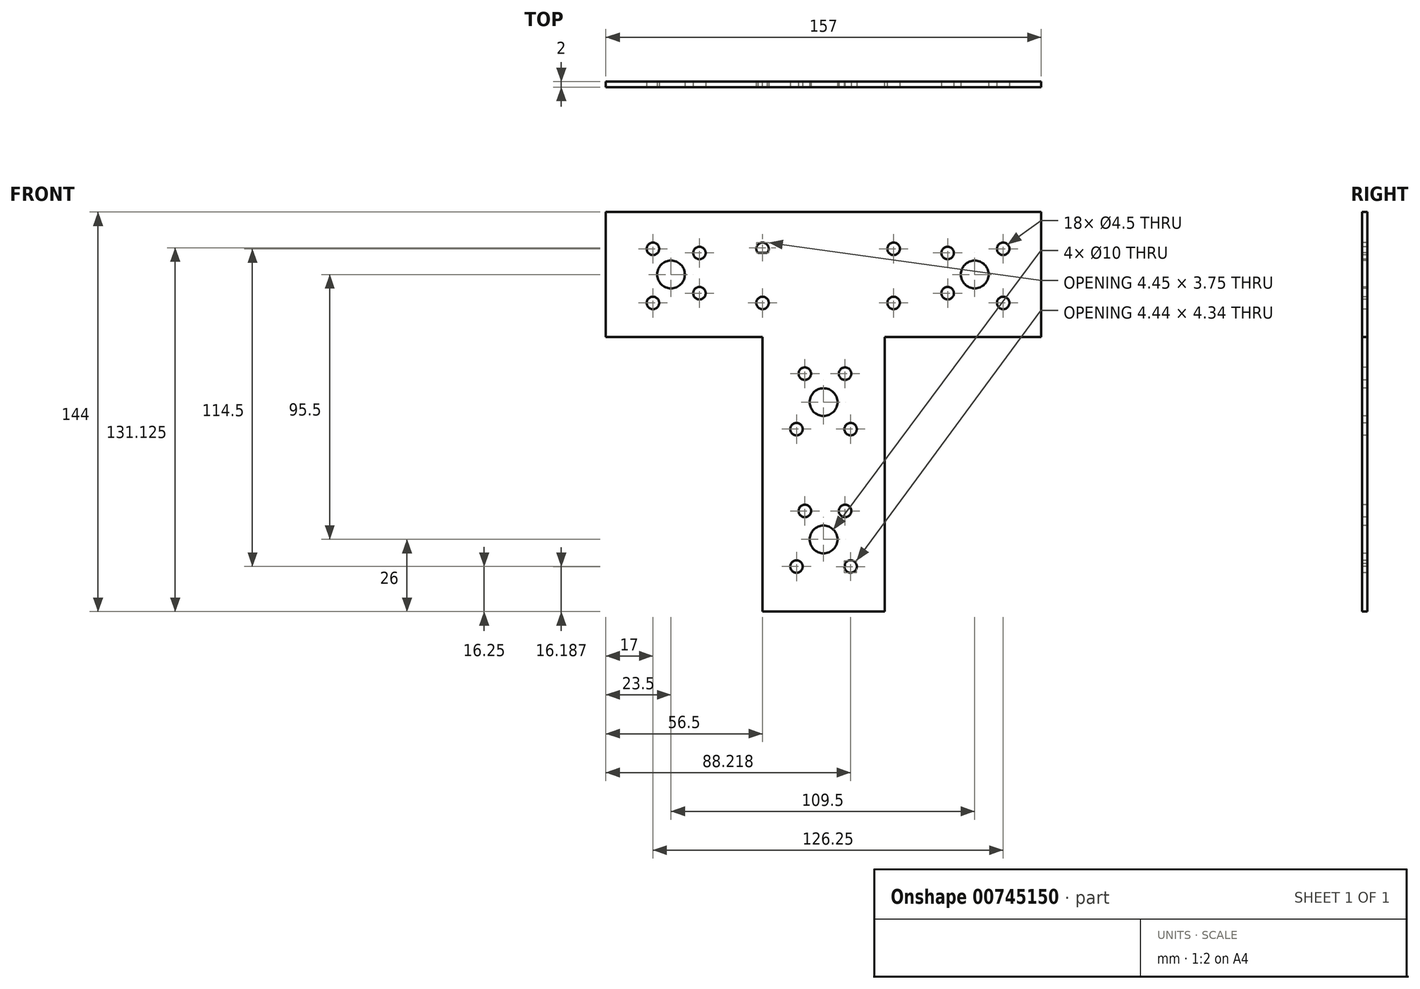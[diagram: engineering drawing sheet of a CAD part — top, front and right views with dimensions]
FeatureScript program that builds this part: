
annotation { "Feature Type Name" : "Feature", "Feature Type Description" : "" }
export const myFeature = defineFeature(function(context is Context, id is Id, definition is map)
    precondition{}
    {
        {
            var Q0;
            Q0=qCreatedBy(makeId("Front.planeOp"),FACE);
            var sketch = newSketch(context, id + "F0", { "sketchPlane" : qUnion([Q0])});
            skLineSegment(sketch, "E0.bottom", {"start": v(-78.5, -22.5) * mm, "end": v(78.5, -22.5) * mm});
            skLineSegment(sketch, "E0.top", {"start": v(-78.5, 22.5) * mm, "end": v(78.5, 22.5) * mm});
            skLineSegment(sketch, "E0.left", {"start": v(-78.5, -22.5) * mm, "end": v(-78.5, 22.5) * mm});
            skLineSegment(sketch, "E0.right", {"start": v(78.5, -22.5) * mm, "end": v(78.5, 22.5) * mm});
            skPoint(sketch, "E0.middle", {"position": v(0, 0) * mm});
            skLineSegment(sketch, "E1", {"start": v(-78.5, -22.5) * mm, "end": v(-22, -22.5) * mm});
            skLineSegment(sketch, "E2", {"start": v(-22, -22.5) * mm, "end": v(22, -22.5) * mm});
            skLineSegment(sketch, "E3", {"start": v(22, -22.5) * mm, "end": v(78.5, -22.5) * mm});
            skLineSegment(sketch, "E4", {"start": v(-22, -22.5) * mm, "end": v(-22, -121.5) * mm});
            skLineSegment(sketch, "E5", {"start": v(-22, -121.5) * mm, "end": v(22, -121.5) * mm});
            skLineSegment(sketch, "E6", {"start": v(22, -121.5) * mm, "end": v(22, -22.5) * mm});
            skSolve(sketch);
        }
        {
            var Q0;
            Q0 = qSketchRegion(id + "F0", true);
            extrude(context, id + "F1", {"entities" : qUnion([Q0]), "depth" : 2 * mm, "offsetDistance" : 25.4 * mm});
        }
        {
            var Q0;
            Q0=makeQuery(id+"F1.opExtrude","CAP_FACE",FACE,{"disambiguationData":[OSD([sQuery(id+"F0.wireOp",EDGE,"E0.top"),sQuery(id+"F0.wireOp",EDGE,"E0.left"),sQuery(id+"F0.wireOp",EDGE,"E0.right"),sQuery(id+"F0.wireOp",EDGE,"E1"),sQuery(id+"F0.wireOp",EDGE,"E3"),sQuery(id+"F0.wireOp",EDGE,"E4"),sQuery(id+"F0.wireOp",EDGE,"E5"),sQuery(id+"F0.wireOp",EDGE,"E6")])],"isStart":false});
            var sketch = newSketch(context, id + "F2", { "sketchPlane" : qUnion([Q0])});
            skLineSegment(sketch, "E7", {"start": v(9.75, -121.5) * mm, "end": v(9.75, -105.25) * mm});
            skLineSegment(sketch, "E8", {"start": v(9.75, -105.25) * mm, "end": v(22, -105.25) * mm});
            skCircle(sketch, "E9", {"center": v(9.75, -105.25) * mm, "radius": 2.25 * mm});
            skLineSegment(sketch, "E10", {"start": v(9.75, -105.25) * mm, "end": v(-9.75, -105.25) * mm});
            skCircle(sketch, "E11", {"center": v(-9.75, -105.25) * mm, "radius": 2.25 * mm});
            skLineSegment(sketch, "E12", {"start": v(22, -95.5) * mm, "end": v(0, -95.5) * mm});
            skLineSegment(sketch, "E13", {"start": v(0, -95.5) * mm, "end": v(0, -121.5) * mm});
            skCircle(sketch, "E14", {"center": v(0, -95.5) * mm, "radius": 5 * mm});
            skLineSegment(sketch, "E15", {"start": v(22, -85.25) * mm, "end": v(7.75, -85.25) * mm});
            skLineSegment(sketch, "E16", {"start": v(7.75, -85.25) * mm, "end": v(7.75, -121.5) * mm});
            skCircle(sketch, "E17", {"center": v(7.75, -85.25) * mm, "radius": 2.25 * mm});
            skLineSegment(sketch, "E18", {"start": v(7.75, -85.25) * mm, "end": v(-6.75, -85.25) * mm});
            skCircle(sketch, "E19", {"center": v(-6.75, -85.25) * mm, "radius": 2.25 * mm});
            skLineSegment(sketch, "E20", {"start": v(9.75, -105.25) * mm, "end": v(9.75, -55.75) * mm});
            skCircle(sketch, "E21", {"center": v(9.75, -55.75) * mm, "radius": 2.25 * mm});
            skLineSegment(sketch, "E22", {"start": v(9.75, -55.75) * mm, "end": v(-9.75, -55.75) * mm});
            skCircle(sketch, "E23", {"center": v(-9.75, -55.75) * mm, "radius": 2.25 * mm});
            skLineSegment(sketch, "E24", {"start": v(0, -95.5) * mm, "end": v(0, -46) * mm});
            skCircle(sketch, "E25", {"center": v(0, -46) * mm, "radius": 5 * mm});
            skLineSegment(sketch, "E26", {"start": v(7.75, -85.25) * mm, "end": v(7.75, -35.75) * mm});
            skCircle(sketch, "E27", {"center": v(7.75, -35.75) * mm, "radius": 2.25 * mm});
            skLineSegment(sketch, "E28", {"start": v(7.75, -35.75) * mm, "end": v(-6.75, -35.75) * mm});
            skCircle(sketch, "E29", {"center": v(-6.75, -35.75) * mm, "radius": 2.25 * mm});
            skLineSegment(sketch, "E30", {"start": v(78.5, -10.25) * mm, "end": v(64.75, -10.25) * mm});
            skLineSegment(sketch, "E31", {"start": v(64.75, -10.25) * mm, "end": v(64.75, -22.5) * mm});
            skCircle(sketch, "E32", {"center": v(64.75, -10.25) * mm, "radius": 2.25 * mm});
            skLineSegment(sketch, "E33", {"start": v(64.75, -10.25) * mm, "end": v(64.75, 9.25) * mm});
            skCircle(sketch, "E34", {"center": v(64.75, 9.25) * mm, "radius": 2.25 * mm});
            skLineSegment(sketch, "E35", {"start": v(78.5, 0) * mm, "end": v(54.5, 0) * mm});
            skLineSegment(sketch, "E36", {"start": v(54.5, 0) * mm, "end": v(54.5, -22.5) * mm});
            skCircle(sketch, "E37", {"center": v(54.5, 0) * mm, "radius": 5 * mm});
            skLineSegment(sketch, "E38", {"start": v(78.5, 7.75) * mm, "end": v(44.75, 7.75) * mm});
            skCircle(sketch, "E39", {"center": v(44.75, 7.75) * mm, "radius": 2.25 * mm});
            skLineSegment(sketch, "E40", {"start": v(44.75, 7.75) * mm, "end": v(44.75, 22.5) * mm});
            skLineSegment(sketch, "E41", {"start": v(44.75, 7.75) * mm, "end": v(44.75, -6.75) * mm});
            skCircle(sketch, "E42", {"center": v(44.75, -6.75) * mm, "radius": 2.25 * mm});
            skLineSegment(sketch, "E43", {"start": v(64.75, 9.25) * mm, "end": v(25.25, 9.25) * mm});
            skCircle(sketch, "E44", {"center": v(25.25, 9.25) * mm, "radius": 2.25 * mm});
            skLineSegment(sketch, "E45", {"start": v(25.25, 9.25) * mm, "end": v(25.25, -10.25) * mm});
            skCircle(sketch, "E46", {"center": v(25.25, -10.25) * mm, "radius": 2.25 * mm});
            skLineSegment(sketch, "E47", {"start": v(25.25, 9.25) * mm, "end": v(-22, 9.25) * mm});
            skCircle(sketch, "E48", {"center": v(-22, 9.25) * mm, "radius": 2.25 * mm});
            skLineSegment(sketch, "E49", {"start": v(25.25, -10.25) * mm, "end": v(-22, -10.25) * mm});
            skCircle(sketch, "E50", {"center": v(-22, -10.25) * mm, "radius": 2.25 * mm});
            skLineSegment(sketch, "E51", {"start": v(-22, 9.25) * mm, "end": v(-61.5, 9.25) * mm});
            skCircle(sketch, "E52", {"center": v(-61.5, 9.25) * mm, "radius": 2.25 * mm});
            skLineSegment(sketch, "E53", {"start": v(-22, -10.25) * mm, "end": v(-61.5, -10.25) * mm});
            skCircle(sketch, "E54", {"center": v(-61.5, -10.25) * mm, "radius": 2.25 * mm});
            skLineSegment(sketch, "E55", {"start": v(44.75, 7.75) * mm, "end": v(-44.75, 7.75) * mm});
            skLineSegment(sketch, "E56", {"start": v(44.75, -6.75) * mm, "end": v(-44.75, -6.75) * mm});
            skCircle(sketch, "E57", {"center": v(-44.75, 7.75) * mm, "radius": 2.25 * mm});
            skCircle(sketch, "E58", {"center": v(-44.75, -6.75) * mm, "radius": 2.25 * mm});
            skLineSegment(sketch, "E59", {"start": v(54.5, 0) * mm, "end": v(-55, 0) * mm});
            skCircle(sketch, "E60", {"center": v(-55, 0) * mm, "radius": 5 * mm});
            skSolve(sketch);
        }
        {
            var Q0;
            Q0=makeQuery(id+"F2.imprint","IMPRINT",FACE,{"disambiguationData":[TD([[makeQuery(id+"F2.imprint","IMPRINT",EDGE,{"derivedFrom":sQuery(id+"F2.wireOp",EDGE,"E11")}),1.0]])]});
            var Q1;
            Q1=makeQuery(id+"F2.imprint","IMPRINT",FACE,{"disambiguationData":[TD([[makeQuery(id+"F2.imprint","IMPRINT",EDGE,{"derivedFrom":sQuery(id+"F2.wireOp",EDGE,"E19")}),1.0]])]});
            var Q2;
            Q2=makeQuery(id+"F2.imprint","IMPRINT",FACE,{"disambiguationData":[TD([[makeQuery(id+"F2.imprint","IMPRINT",EDGE,{"derivedFrom":sQuery(id+"F2.wireOp",EDGE,"E23")}),1.0]])]});
            var Q3;
            Q3=makeQuery(id+"F2.imprint","IMPRINT",FACE,{"disambiguationData":[TD([[makeQuery(id+"F2.imprint","IMPRINT",EDGE,{"derivedFrom":sQuery(id+"F2.wireOp",EDGE,"E25")}),1.0]])]});
            var Q4;
            Q4=makeQuery(id+"F2.imprint","IMPRINT",FACE,{"disambiguationData":[TD([[makeQuery(id+"F2.imprint","IMPRINT",EDGE,{"derivedFrom":sQuery(id+"F2.wireOp",EDGE,"E29")}),1.0]])]});
            var Q5;
            Q5=makeQuery(id+"F2.imprint","IMPRINT",FACE,{"disambiguationData":[TD([[makeQuery(id+"F2.imprint","IMPRINT",EDGE,{"derivedFrom":sQuery(id+"F2.wireOp",EDGE,"E52")}),1.0]])]});
            var Q6;
            Q6=makeQuery(id+"F2.imprint","IMPRINT",FACE,{"disambiguationData":[TD([[makeQuery(id+"F2.imprint","IMPRINT",EDGE,{"derivedFrom":sQuery(id+"F2.wireOp",EDGE,"E54")}),1.0]])]});
            var Q7;
            Q7=makeQuery(id+"F2.imprint","IMPRINT",FACE,{"disambiguationData":[TD([[makeQuery(id+"F2.imprint","IMPRINT",EDGE,{"derivedFrom":sQuery(id+"F2.wireOp",EDGE,"E58")}),1.0]])]});
            var Q8;
            Q8=makeQuery(id+"F2.imprint","IMPRINT",FACE,{"disambiguationData":[TD([[makeQuery(id+"F2.imprint","IMPRINT",EDGE,{"derivedFrom":sQuery(id+"F2.wireOp",EDGE,"E60")}),1.0]])]});
            var Q9;
            {var subQ0=sQuery(id+"F2.wireOp",EDGE,"E28");var subQ1=sQuery(id+"F2.wireOp",EDGE,"E26");var subQ2=makeQuery(id+"F2.imprint","INTERSECT",VERTEX,{"derivedFrom":[subQ1,subQ0]});Q9=makeQuery(id+"F2.imprint","IMPRINT",FACE,{"disambiguationData":[TD([[makeQuery(id+"F2.imprint","IMPRINT",EDGE,{"disambiguationData":[TD([[subQ2,1.0]])],"derivedFrom":subQ1}),1.0]])]});}
            var Q10;
            {var subQ0=sQuery(id+"F2.wireOp",EDGE,"E28");var subQ1=sQuery(id+"F2.wireOp",EDGE,"E26");var subQ2=makeQuery(id+"F2.imprint","INTERSECT",VERTEX,{"derivedFrom":[subQ1,subQ0]});Q10=makeQuery(id+"F2.imprint","IMPRINT",FACE,{"disambiguationData":[TD([[makeQuery(id+"F2.imprint","IMPRINT",EDGE,{"disambiguationData":[TD([[subQ2,1.0]])],"derivedFrom":subQ1}),-1.0]])]});}
            var Q11;
            {var subQ0=sQuery(id+"F2.wireOp",EDGE,"E56");var subQ1=sQuery(id+"F2.wireOp",EDGE,"E41");var subQ2=makeQuery(id+"F2.imprint","INTERSECT",VERTEX,{"derivedFrom":[subQ1,subQ0]});Q11=makeQuery(id+"F2.imprint","IMPRINT",FACE,{"disambiguationData":[TD([[makeQuery(id+"F2.imprint","IMPRINT",EDGE,{"disambiguationData":[TD([[subQ2,1.0]])],"derivedFrom":subQ1}),-1.0]])]});}
            var Q12;
            {var subQ0=sQuery(id+"F2.wireOp",EDGE,"E56");var subQ1=sQuery(id+"F2.wireOp",EDGE,"E41");var subQ2=makeQuery(id+"F2.imprint","INTERSECT",VERTEX,{"derivedFrom":[subQ1,subQ0]});Q12=makeQuery(id+"F2.imprint","IMPRINT",FACE,{"disambiguationData":[TD([[makeQuery(id+"F2.imprint","IMPRINT",EDGE,{"disambiguationData":[TD([[subQ2,1.0]])],"derivedFrom":subQ1}),1.0]])]});}
            var Q13;
            {var subQ0=sQuery(id+"F2.wireOp",EDGE,"E49");var subQ1=sQuery(id+"F2.wireOp",EDGE,"E45");var subQ2=makeQuery(id+"F2.imprint","INTERSECT",VERTEX,{"derivedFrom":[subQ1,subQ0]});Q13=makeQuery(id+"F2.imprint","IMPRINT",FACE,{"disambiguationData":[TD([[makeQuery(id+"F2.imprint","IMPRINT",EDGE,{"disambiguationData":[TD([[subQ2,1.0]])],"derivedFrom":subQ1}),-1.0]])]});}
            var Q14;
            {var subQ0=sQuery(id+"F2.wireOp",EDGE,"E49");var subQ1=sQuery(id+"F2.wireOp",EDGE,"E45");var subQ2=makeQuery(id+"F2.imprint","INTERSECT",VERTEX,{"derivedFrom":[subQ1,subQ0]});Q14=makeQuery(id+"F2.imprint","IMPRINT",FACE,{"disambiguationData":[TD([[makeQuery(id+"F2.imprint","IMPRINT",EDGE,{"disambiguationData":[TD([[subQ2,1.0]])],"derivedFrom":subQ1}),1.0]])]});}
            var Q15;
            {var subQ0=sQuery(id+"F2.wireOp",EDGE,"E51");var subQ1=sQuery(id+"F2.wireOp",EDGE,"E47");var subQ2=makeQuery(id+"F2.imprint","INTERSECT",VERTEX,{"derivedFrom":[subQ1,subQ0]});Q15=makeQuery(id+"F2.imprint","IMPRINT",FACE,{"disambiguationData":[TD([[makeQuery(id+"F2.imprint","IMPRINT",EDGE,{"disambiguationData":[TD([[subQ2,1.0]])],"derivedFrom":subQ1}),-1.0]])]});}
            var Q16;
            {var subQ0=sQuery(id+"F2.wireOp",EDGE,"E55");var subQ1=sQuery(id+"F2.wireOp",EDGE,"E48");var subQ2=makeQuery(id+"F2.imprint","INTERSECT",VERTEX,{"disambiguationData":[OD(0.0)],"derivedFrom":[subQ1,subQ0]});Q16=makeQuery(id+"F2.imprint","IMPRINT",FACE,{"disambiguationData":[TD([[makeQuery(id+"F2.imprint","IMPRINT",EDGE,{"disambiguationData":[TD([[subQ2,-1.0]])],"derivedFrom":subQ1}),1.0]])]});}
            var Q17;
            {var subQ0=sQuery(id+"F2.wireOp",EDGE,"E53");var subQ1=sQuery(id+"F2.wireOp",EDGE,"E49");var subQ2=makeQuery(id+"F2.imprint","INTERSECT",VERTEX,{"derivedFrom":[subQ1,subQ0]});Q17=makeQuery(id+"F2.imprint","IMPRINT",FACE,{"disambiguationData":[TD([[makeQuery(id+"F2.imprint","IMPRINT",EDGE,{"disambiguationData":[TD([[subQ2,1.0]])],"derivedFrom":subQ1}),-1.0]])]});}
            var Q18;
            {var subQ0=sQuery(id+"F2.wireOp",EDGE,"E53");var subQ1=sQuery(id+"F2.wireOp",EDGE,"E49");var subQ2=makeQuery(id+"F2.imprint","INTERSECT",VERTEX,{"derivedFrom":[subQ1,subQ0]});Q18=makeQuery(id+"F2.imprint","IMPRINT",FACE,{"disambiguationData":[TD([[makeQuery(id+"F2.imprint","IMPRINT",EDGE,{"disambiguationData":[TD([[subQ2,1.0]])],"derivedFrom":subQ1}),1.0]])]});}
            var Q19;
            {var subQ0=sQuery(id+"F2.wireOp",EDGE,"E57");var subQ1=sQuery(id+"F2.wireOp",EDGE,"E51");var subQ2=makeQuery(id+"F2.imprint","INTERSECT",VERTEX,{"disambiguationData":[OD(0.0)],"derivedFrom":[subQ1,subQ0]});Q19=makeQuery(id+"F2.imprint","IMPRINT",FACE,{"disambiguationData":[TD([[makeQuery(id+"F2.imprint","IMPRINT",EDGE,{"disambiguationData":[TD([[subQ2,1.0]])],"derivedFrom":subQ1}),-1.0]])]});}
            var Q20;
            {var subQ1=sQuery(id+"F2.wireOp",EDGE,"E7");var subQ3=sQuery(id+"F2.wireOp",EDGE,"E9");var subQ4=makeQuery(id+"F2.imprint","INTERSECT",VERTEX,{"derivedFrom":[subQ1,subQ3]});Q20=makeQuery(id+"F2.imprint","IMPRINT",FACE,{"disambiguationData":[TD([[makeQuery(id+"F2.imprint","IMPRINT",EDGE,{"disambiguationData":[TD([[subQ4,-1.0]])],"derivedFrom":subQ3}),1.0]])]});}
            var Q21;
            {var subQ1=sQuery(id+"F2.wireOp",EDGE,"E8");var subQ3=sQuery(id+"F2.wireOp",EDGE,"E9");var subQ4=makeQuery(id+"F2.imprint","INTERSECT",VERTEX,{"derivedFrom":[subQ1,subQ3]});Q21=makeQuery(id+"F2.imprint","IMPRINT",FACE,{"disambiguationData":[TD([[makeQuery(id+"F2.imprint","IMPRINT",EDGE,{"disambiguationData":[TD([[subQ4,-1.0]])],"derivedFrom":subQ3}),1.0]])]});}
            var Q22;
            {var subQ0=sQuery(id+"F2.wireOp",EDGE,"E16");var subQ1=sQuery(id+"F2.wireOp",EDGE,"E9");var subQ2=makeQuery(id+"F2.imprint","INTERSECT",VERTEX,{"disambiguationData":[OD(0.0)],"derivedFrom":[subQ1,subQ0]});Q22=makeQuery(id+"F2.imprint","IMPRINT",FACE,{"disambiguationData":[TD([[makeQuery(id+"F2.imprint","IMPRINT",EDGE,{"disambiguationData":[TD([[subQ2,-1.0]])],"derivedFrom":subQ1}),1.0]])]});}
            var Q23;
            {var subQ0=sQuery(id+"F2.wireOp",EDGE,"E10");var subQ1=sQuery(id+"F2.wireOp",EDGE,"E9");var subQ2=makeQuery(id+"F2.imprint","INTERSECT",VERTEX,{"derivedFrom":[subQ1,subQ0]});Q23=makeQuery(id+"F2.imprint","IMPRINT",FACE,{"disambiguationData":[TD([[makeQuery(id+"F2.imprint","IMPRINT",EDGE,{"disambiguationData":[TD([[subQ2,-1.0]])],"derivedFrom":subQ1}),1.0]])]});}
            var Q24;
            {var subQ1=sQuery(id+"F2.wireOp",EDGE,"E12");var subQ3=sQuery(id+"F2.wireOp",EDGE,"E14");var subQ4=makeQuery(id+"F2.imprint","INTERSECT",VERTEX,{"derivedFrom":[subQ1,subQ3]});Q24=makeQuery(id+"F2.imprint","IMPRINT",FACE,{"disambiguationData":[TD([[makeQuery(id+"F2.imprint","IMPRINT",EDGE,{"disambiguationData":[TD([[subQ4,1.0]])],"derivedFrom":subQ3}),1.0]])]});}
            var Q25;
            {var subQ1=sQuery(id+"F2.wireOp",EDGE,"E12");var subQ3=sQuery(id+"F2.wireOp",EDGE,"E14");var subQ4=makeQuery(id+"F2.imprint","INTERSECT",VERTEX,{"derivedFrom":[subQ1,subQ3]});Q25=makeQuery(id+"F2.imprint","IMPRINT",FACE,{"disambiguationData":[TD([[makeQuery(id+"F2.imprint","IMPRINT",EDGE,{"disambiguationData":[TD([[subQ4,-1.0]])],"derivedFrom":subQ3}),1.0]])]});}
            var Q26;
            {var subQ1=sQuery(id+"F2.wireOp",EDGE,"E13");var subQ3=sQuery(id+"F2.wireOp",EDGE,"E14");var subQ4=makeQuery(id+"F2.imprint","INTERSECT",VERTEX,{"derivedFrom":[subQ1,subQ3]});Q26=makeQuery(id+"F2.imprint","IMPRINT",FACE,{"disambiguationData":[TD([[makeQuery(id+"F2.imprint","IMPRINT",EDGE,{"disambiguationData":[TD([[subQ4,1.0]])],"derivedFrom":subQ3}),1.0]])]});}
            var Q27;
            {var subQ0=sQuery(id+"F2.wireOp",EDGE,"E17");var subQ1=sQuery(id+"F2.wireOp",EDGE,"E15");var subQ2=makeQuery(id+"F2.imprint","INTERSECT",VERTEX,{"derivedFrom":[subQ1,subQ0]});Q27=makeQuery(id+"F2.imprint","IMPRINT",FACE,{"disambiguationData":[TD([[makeQuery(id+"F2.imprint","IMPRINT",EDGE,{"disambiguationData":[TD([[subQ2,-1.0]])],"derivedFrom":subQ1}),-1.0]])]});}
            var Q28;
            {var subQ0=sQuery(id+"F2.wireOp",EDGE,"E17");var subQ1=sQuery(id+"F2.wireOp",EDGE,"E15");var subQ2=makeQuery(id+"F2.imprint","INTERSECT",VERTEX,{"derivedFrom":[subQ1,subQ0]});Q28=makeQuery(id+"F2.imprint","IMPRINT",FACE,{"disambiguationData":[TD([[makeQuery(id+"F2.imprint","IMPRINT",EDGE,{"disambiguationData":[TD([[subQ2,-1.0]])],"derivedFrom":subQ1}),1.0]])]});}
            var Q29;
            {var subQ0=sQuery(id+"F2.wireOp",EDGE,"E22");var subQ1=sQuery(id+"F2.wireOp",EDGE,"E20");var subQ2=makeQuery(id+"F2.imprint","INTERSECT",VERTEX,{"derivedFrom":[subQ1,subQ0]});Q29=makeQuery(id+"F2.imprint","IMPRINT",FACE,{"disambiguationData":[TD([[makeQuery(id+"F2.imprint","IMPRINT",EDGE,{"disambiguationData":[TD([[subQ2,1.0]])],"derivedFrom":subQ1}),1.0]])]});}
            var Q30;
            {var subQ0=sQuery(id+"F2.wireOp",EDGE,"E22");var subQ1=sQuery(id+"F2.wireOp",EDGE,"E20");var subQ2=makeQuery(id+"F2.imprint","INTERSECT",VERTEX,{"derivedFrom":[subQ1,subQ0]});Q30=makeQuery(id+"F2.imprint","IMPRINT",FACE,{"disambiguationData":[TD([[makeQuery(id+"F2.imprint","IMPRINT",EDGE,{"disambiguationData":[TD([[subQ2,1.0]])],"derivedFrom":subQ1}),-1.0]])]});}
            var Q31;
            {var subQ0=sQuery(id+"F2.wireOp",EDGE,"E26");var subQ1=sQuery(id+"F2.wireOp",EDGE,"E21");var subQ2=makeQuery(id+"F2.imprint","INTERSECT",VERTEX,{"disambiguationData":[OD(0.0)],"derivedFrom":[subQ1,subQ0]});Q31=makeQuery(id+"F2.imprint","IMPRINT",FACE,{"disambiguationData":[TD([[makeQuery(id+"F2.imprint","IMPRINT",EDGE,{"disambiguationData":[TD([[subQ2,-1.0]])],"derivedFrom":subQ1}),1.0]])]});}
            var Q32;
            {var subQ0=sQuery(id+"F2.wireOp",EDGE,"E22");var subQ1=sQuery(id+"F2.wireOp",EDGE,"E21");var subQ2=makeQuery(id+"F2.imprint","INTERSECT",VERTEX,{"derivedFrom":[subQ1,subQ0]});Q32=makeQuery(id+"F2.imprint","IMPRINT",FACE,{"disambiguationData":[TD([[makeQuery(id+"F2.imprint","IMPRINT",EDGE,{"disambiguationData":[TD([[subQ2,-1.0]])],"derivedFrom":subQ1}),1.0]])]});}
            var Q33;
            {var subQ1=sQuery(id+"F2.wireOp",EDGE,"E30");var subQ3=sQuery(id+"F2.wireOp",EDGE,"E32");var subQ4=makeQuery(id+"F2.imprint","INTERSECT",VERTEX,{"derivedFrom":[subQ1,subQ3]});Q33=makeQuery(id+"F2.imprint","IMPRINT",FACE,{"disambiguationData":[TD([[makeQuery(id+"F2.imprint","IMPRINT",EDGE,{"disambiguationData":[TD([[subQ4,1.0]])],"derivedFrom":subQ3}),1.0]])]});}
            var Q34;
            {var subQ1=sQuery(id+"F2.wireOp",EDGE,"E30");var subQ3=sQuery(id+"F2.wireOp",EDGE,"E32");var subQ4=makeQuery(id+"F2.imprint","INTERSECT",VERTEX,{"derivedFrom":[subQ1,subQ3]});Q34=makeQuery(id+"F2.imprint","IMPRINT",FACE,{"disambiguationData":[TD([[makeQuery(id+"F2.imprint","IMPRINT",EDGE,{"disambiguationData":[TD([[subQ4,-1.0]])],"derivedFrom":subQ3}),1.0]])]});}
            var Q35;
            {var subQ1=sQuery(id+"F2.wireOp",EDGE,"E31");var subQ3=sQuery(id+"F2.wireOp",EDGE,"E32");var subQ4=makeQuery(id+"F2.imprint","INTERSECT",VERTEX,{"derivedFrom":[subQ1,subQ3]});Q35=makeQuery(id+"F2.imprint","IMPRINT",FACE,{"disambiguationData":[TD([[makeQuery(id+"F2.imprint","IMPRINT",EDGE,{"disambiguationData":[TD([[subQ4,1.0]])],"derivedFrom":subQ3}),1.0]])]});}
            var Q36;
            {var subQ0=sQuery(id+"F2.wireOp",EDGE,"E34");var subQ1=sQuery(id+"F2.wireOp",EDGE,"E33");var subQ2=makeQuery(id+"F2.imprint","INTERSECT",VERTEX,{"derivedFrom":[subQ1,subQ0]});Q36=makeQuery(id+"F2.imprint","IMPRINT",FACE,{"disambiguationData":[TD([[makeQuery(id+"F2.imprint","IMPRINT",EDGE,{"disambiguationData":[TD([[subQ2,-1.0]])],"derivedFrom":subQ1}),1.0]])]});}
            var Q37;
            {var subQ0=sQuery(id+"F2.wireOp",EDGE,"E34");var subQ1=sQuery(id+"F2.wireOp",EDGE,"E33");var subQ2=makeQuery(id+"F2.imprint","INTERSECT",VERTEX,{"derivedFrom":[subQ1,subQ0]});Q37=makeQuery(id+"F2.imprint","IMPRINT",FACE,{"disambiguationData":[TD([[makeQuery(id+"F2.imprint","IMPRINT",EDGE,{"disambiguationData":[TD([[subQ2,-1.0]])],"derivedFrom":subQ1}),-1.0]])]});}
            var Q38;
            {var subQ0=sQuery(id+"F2.wireOp",EDGE,"E43");var subQ1=sQuery(id+"F2.wireOp",EDGE,"E33");var subQ2=makeQuery(id+"F2.imprint","INTERSECT",VERTEX,{"derivedFrom":[subQ1,subQ0]});Q38=makeQuery(id+"F2.imprint","IMPRINT",FACE,{"disambiguationData":[TD([[makeQuery(id+"F2.imprint","IMPRINT",EDGE,{"disambiguationData":[TD([[subQ2,1.0]])],"derivedFrom":subQ1}),1.0]])]});}
            var Q39;
            {var subQ0=sQuery(id+"F2.wireOp",EDGE,"E43");var subQ1=sQuery(id+"F2.wireOp",EDGE,"E33");var subQ2=makeQuery(id+"F2.imprint","INTERSECT",VERTEX,{"derivedFrom":[subQ1,subQ0]});Q39=makeQuery(id+"F2.imprint","IMPRINT",FACE,{"disambiguationData":[TD([[makeQuery(id+"F2.imprint","IMPRINT",EDGE,{"disambiguationData":[TD([[subQ2,1.0]])],"derivedFrom":subQ1}),-1.0]])]});}
            var Q40;
            {var subQ1=sQuery(id+"F2.wireOp",EDGE,"E35");var subQ3=sQuery(id+"F2.wireOp",EDGE,"E37");var subQ4=makeQuery(id+"F2.imprint","INTERSECT",VERTEX,{"derivedFrom":[subQ1,subQ3]});Q40=makeQuery(id+"F2.imprint","IMPRINT",FACE,{"disambiguationData":[TD([[makeQuery(id+"F2.imprint","IMPRINT",EDGE,{"disambiguationData":[TD([[subQ4,1.0]])],"derivedFrom":subQ3}),1.0]])]});}
            var Q41;
            {var subQ1=sQuery(id+"F2.wireOp",EDGE,"E35");var subQ3=sQuery(id+"F2.wireOp",EDGE,"E37");var subQ4=makeQuery(id+"F2.imprint","INTERSECT",VERTEX,{"derivedFrom":[subQ1,subQ3]});Q41=makeQuery(id+"F2.imprint","IMPRINT",FACE,{"disambiguationData":[TD([[makeQuery(id+"F2.imprint","IMPRINT",EDGE,{"disambiguationData":[TD([[subQ4,-1.0]])],"derivedFrom":subQ3}),1.0]])]});}
            var Q42;
            {var subQ1=sQuery(id+"F2.wireOp",EDGE,"E36");var subQ3=sQuery(id+"F2.wireOp",EDGE,"E37");var subQ4=makeQuery(id+"F2.imprint","INTERSECT",VERTEX,{"derivedFrom":[subQ1,subQ3]});Q42=makeQuery(id+"F2.imprint","IMPRINT",FACE,{"disambiguationData":[TD([[makeQuery(id+"F2.imprint","IMPRINT",EDGE,{"disambiguationData":[TD([[subQ4,1.0]])],"derivedFrom":subQ3}),1.0]])]});}
            var Q43;
            {var subQ0=sQuery(id+"F2.wireOp",EDGE,"E43");var subQ1=sQuery(id+"F2.wireOp",EDGE,"E39");var subQ2=makeQuery(id+"F2.imprint","INTERSECT",VERTEX,{"disambiguationData":[OD(0.0)],"derivedFrom":[subQ1,subQ0]});Q43=makeQuery(id+"F2.imprint","IMPRINT",FACE,{"disambiguationData":[TD([[makeQuery(id+"F2.imprint","IMPRINT",EDGE,{"disambiguationData":[TD([[subQ2,-1.0]])],"derivedFrom":subQ1}),1.0]])]});}
            var Q44;
            {var subQ0=sQuery(id+"F2.wireOp",EDGE,"E40");var subQ1=sQuery(id+"F2.wireOp",EDGE,"E39");var subQ2=makeQuery(id+"F2.imprint","INTERSECT",VERTEX,{"derivedFrom":[subQ1,subQ0]});Q44=makeQuery(id+"F2.imprint","IMPRINT",FACE,{"disambiguationData":[TD([[makeQuery(id+"F2.imprint","IMPRINT",EDGE,{"disambiguationData":[TD([[subQ2,-1.0]])],"derivedFrom":subQ1}),1.0]])]});}
            var Q45;
            {var subQ1=sQuery(id+"F2.wireOp",EDGE,"E43");var subQ3=sQuery(id+"F2.wireOp",EDGE,"E44");var subQ4=makeQuery(id+"F2.imprint","INTERSECT",VERTEX,{"derivedFrom":[subQ1,subQ3]});Q45=makeQuery(id+"F2.imprint","IMPRINT",FACE,{"disambiguationData":[TD([[makeQuery(id+"F2.imprint","IMPRINT",EDGE,{"disambiguationData":[TD([[subQ4,-1.0]])],"derivedFrom":subQ3}),1.0]])]});}
            var Q46;
            {var subQ0=sQuery(id+"F2.wireOp",EDGE,"E55");var subQ1=sQuery(id+"F2.wireOp",EDGE,"E44");var subQ2=makeQuery(id+"F2.imprint","INTERSECT",VERTEX,{"disambiguationData":[OD(0.0)],"derivedFrom":[subQ1,subQ0]});Q46=makeQuery(id+"F2.imprint","IMPRINT",FACE,{"disambiguationData":[TD([[makeQuery(id+"F2.imprint","IMPRINT",EDGE,{"disambiguationData":[TD([[subQ2,-1.0]])],"derivedFrom":subQ1}),1.0]])]});}
            var Q47;
            {var subQ0=sQuery(id+"F2.wireOp",EDGE,"E45");var subQ1=sQuery(id+"F2.wireOp",EDGE,"E44");var subQ2=makeQuery(id+"F2.imprint","INTERSECT",VERTEX,{"derivedFrom":[subQ1,subQ0]});Q47=makeQuery(id+"F2.imprint","IMPRINT",FACE,{"disambiguationData":[TD([[makeQuery(id+"F2.imprint","IMPRINT",EDGE,{"disambiguationData":[TD([[subQ2,-1.0]])],"derivedFrom":subQ1}),1.0]])]});}
            var Q48;
            {var subQ0=sQuery(id+"F2.wireOp",EDGE,"E57");var subQ1=sQuery(id+"F2.wireOp",EDGE,"E51");var subQ2=makeQuery(id+"F2.imprint","INTERSECT",VERTEX,{"disambiguationData":[OD(0.0)],"derivedFrom":[subQ1,subQ0]});Q48=makeQuery(id+"F2.imprint","IMPRINT",FACE,{"disambiguationData":[TD([[makeQuery(id+"F2.imprint","IMPRINT",EDGE,{"disambiguationData":[TD([[subQ2,1.0]])],"derivedFrom":subQ1}),1.0]])]});}
            var Q49;
            {var subQ1=sQuery(id+"F2.wireOp",EDGE,"E7");var subQ3=sQuery(id+"F2.wireOp",EDGE,"E9");var subQ4=makeQuery(id+"F2.imprint","INTERSECT",VERTEX,{"derivedFrom":[subQ1,subQ3]});Q49=makeQuery(id+"F2.imprint","IMPRINT",FACE,{"disambiguationData":[TD([[makeQuery(id+"F2.imprint","IMPRINT",EDGE,{"disambiguationData":[TD([[subQ4,1.0]])],"derivedFrom":subQ3}),1.0]])]});}
            var Q50;
            {var subQ0=sQuery(id+"F2.wireOp",EDGE,"E20");var subQ1=sQuery(id+"F2.wireOp",EDGE,"E9");var subQ2=makeQuery(id+"F2.imprint","INTERSECT",VERTEX,{"derivedFrom":[subQ1,subQ0]});Q50=makeQuery(id+"F2.imprint","IMPRINT",FACE,{"disambiguationData":[TD([[makeQuery(id+"F2.imprint","IMPRINT",EDGE,{"disambiguationData":[TD([[subQ2,-1.0]])],"derivedFrom":subQ1}),1.0]])]});}
            var Q51;
            {var subQ0=sQuery(id+"F2.wireOp",EDGE,"E16");var subQ5=sQuery(id+"F2.wireOp",EDGE,"E17");var subQ6=makeQuery(id+"F2.imprint","INTERSECT",VERTEX,{"derivedFrom":[subQ0,subQ5]});Q51=makeQuery(id+"F2.imprint","IMPRINT",FACE,{"disambiguationData":[TD([[makeQuery(id+"F2.imprint","IMPRINT",EDGE,{"disambiguationData":[TD([[subQ6,-1.0]])],"derivedFrom":subQ5}),1.0]])]});}
            var Q52;
            {var subQ3=sQuery(id+"F2.wireOp",EDGE,"E20");var subQ5=sQuery(id+"F2.wireOp",EDGE,"E17");var subQ6=makeQuery(id+"F2.imprint","INTERSECT",VERTEX,{"disambiguationData":[OD(0.0)],"derivedFrom":[subQ5,subQ3]});Q52=makeQuery(id+"F2.imprint","IMPRINT",FACE,{"disambiguationData":[TD([[makeQuery(id+"F2.imprint","IMPRINT",EDGE,{"disambiguationData":[TD([[subQ6,-1.0]])],"derivedFrom":subQ5}),1.0]])]});}
            var Q53;
            {var subQ1=sQuery(id+"F2.wireOp",EDGE,"E38");var subQ3=sQuery(id+"F2.wireOp",EDGE,"E39");var subQ4=makeQuery(id+"F2.imprint","INTERSECT",VERTEX,{"derivedFrom":[subQ1,subQ3]});Q53=makeQuery(id+"F2.imprint","IMPRINT",FACE,{"disambiguationData":[TD([[makeQuery(id+"F2.imprint","IMPRINT",EDGE,{"disambiguationData":[TD([[subQ4,-1.0]])],"derivedFrom":subQ3}),1.0]])]});}
            var Q54;
            {var subQ0=sQuery(id+"F2.wireOp",EDGE,"E43");var subQ1=sQuery(id+"F2.wireOp",EDGE,"E39");var subQ2=makeQuery(id+"F2.imprint","INTERSECT",VERTEX,{"disambiguationData":[OD(1.0)],"derivedFrom":[subQ1,subQ0]});Q54=makeQuery(id+"F2.imprint","IMPRINT",FACE,{"disambiguationData":[TD([[makeQuery(id+"F2.imprint","IMPRINT",EDGE,{"disambiguationData":[TD([[subQ2,-1.0]])],"derivedFrom":subQ1}),1.0]])]});}
            var Q55;
            {var subQ1=sQuery(id+"F2.wireOp",EDGE,"E43");var subQ3=sQuery(id+"F2.wireOp",EDGE,"E44");var subQ4=makeQuery(id+"F2.imprint","INTERSECT",VERTEX,{"derivedFrom":[subQ1,subQ3]});Q55=makeQuery(id+"F2.imprint","IMPRINT",FACE,{"disambiguationData":[TD([[makeQuery(id+"F2.imprint","IMPRINT",EDGE,{"disambiguationData":[TD([[subQ4,1.0]])],"derivedFrom":subQ3}),1.0]])]});}
            var Q56;
            {var subQ0=sQuery(id+"F2.wireOp",EDGE,"E47");var subQ1=sQuery(id+"F2.wireOp",EDGE,"E44");var subQ2=makeQuery(id+"F2.imprint","INTERSECT",VERTEX,{"derivedFrom":[subQ1,subQ0]});Q56=makeQuery(id+"F2.imprint","IMPRINT",FACE,{"disambiguationData":[TD([[makeQuery(id+"F2.imprint","IMPRINT",EDGE,{"disambiguationData":[TD([[subQ2,-1.0]])],"derivedFrom":subQ1}),1.0]])]});}
            var Q57;
            {var subQ0=sQuery(id+"F2.wireOp",EDGE,"E51");var subQ1=sQuery(id+"F2.wireOp",EDGE,"E47");var subQ2=makeQuery(id+"F2.imprint","INTERSECT",VERTEX,{"derivedFrom":[subQ1,subQ0]});Q57=makeQuery(id+"F2.imprint","IMPRINT",FACE,{"disambiguationData":[TD([[makeQuery(id+"F2.imprint","IMPRINT",EDGE,{"disambiguationData":[TD([[subQ2,1.0]])],"derivedFrom":subQ1}),1.0]])]});}
            var Q58;
            {var subQ1=sQuery(id+"F2.wireOp",EDGE,"E16");var subQ3=sQuery(id+"F2.wireOp",EDGE,"E17");var subQ4=makeQuery(id+"F2.imprint","INTERSECT",VERTEX,{"derivedFrom":[subQ1,subQ3]});Q58=makeQuery(id+"F2.imprint","IMPRINT",FACE,{"disambiguationData":[TD([[makeQuery(id+"F2.imprint","IMPRINT",EDGE,{"disambiguationData":[TD([[subQ4,1.0]])],"derivedFrom":subQ3}),1.0]])]});}
            var Q59;
            {var subQ0=sQuery(id+"F2.wireOp",EDGE,"E26");var subQ1=sQuery(id+"F2.wireOp",EDGE,"E17");var subQ2=makeQuery(id+"F2.imprint","INTERSECT",VERTEX,{"derivedFrom":[subQ1,subQ0]});Q59=makeQuery(id+"F2.imprint","IMPRINT",FACE,{"disambiguationData":[TD([[makeQuery(id+"F2.imprint","IMPRINT",EDGE,{"disambiguationData":[TD([[subQ2,-1.0]])],"derivedFrom":subQ1}),1.0]])]});}
            var Q60;
            {var subQ1=sQuery(id+"F2.wireOp",EDGE,"E38");var subQ3=sQuery(id+"F2.wireOp",EDGE,"E39");var subQ4=makeQuery(id+"F2.imprint","INTERSECT",VERTEX,{"derivedFrom":[subQ1,subQ3]});Q60=makeQuery(id+"F2.imprint","IMPRINT",FACE,{"disambiguationData":[TD([[makeQuery(id+"F2.imprint","IMPRINT",EDGE,{"disambiguationData":[TD([[subQ4,1.0]])],"derivedFrom":subQ3}),1.0]])]});}
            var Q61;
            {var subQ0=sQuery(id+"F2.wireOp",EDGE,"E55");var subQ1=sQuery(id+"F2.wireOp",EDGE,"E39");var subQ2=makeQuery(id+"F2.imprint","INTERSECT",VERTEX,{"derivedFrom":[subQ1,subQ0]});Q61=makeQuery(id+"F2.imprint","IMPRINT",FACE,{"disambiguationData":[TD([[makeQuery(id+"F2.imprint","IMPRINT",EDGE,{"disambiguationData":[TD([[subQ2,-1.0]])],"derivedFrom":subQ1}),1.0]])]});}
            extrude(context, id + "F3", {"entities" : qUnion([Q0, Q1, Q2, Q3, Q4, Q5, Q6, Q7, Q8, Q9, Q10, Q11, Q12, Q13, Q14, Q15, Q16, Q17, Q18, Q19, Q20, Q21, Q22, Q23, Q24, Q25, Q26, Q27, Q28, Q29, Q30, Q31, Q32, Q33, Q34, Q35, Q36, Q37, Q38, Q39, Q40, Q41, Q42, Q43, Q44, Q45, Q46, Q47, Q48, Q49, Q50, Q51, Q52, Q53, Q54, Q55, Q56, Q57, Q58, Q59, Q60, Q61]), "operationType" : NewBodyOperationType.REMOVE, "endBound" : BoundingType.THROUGH_ALL, "oppositeDirection" : true, "depth" : 25.4 * mm, "offsetDistance" : 25.4 * mm});
        }
    });
